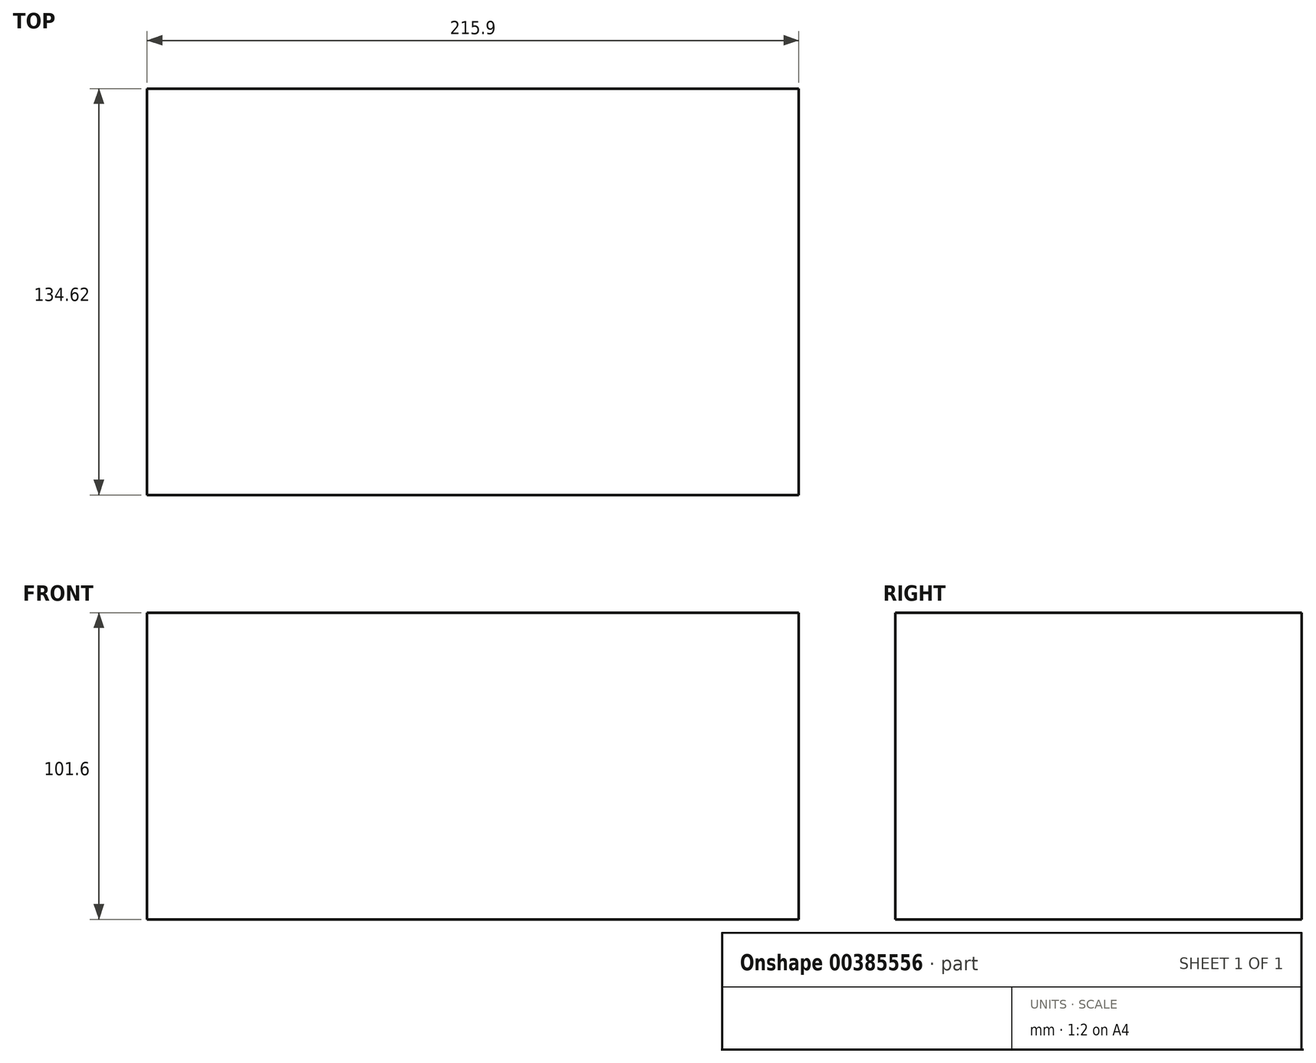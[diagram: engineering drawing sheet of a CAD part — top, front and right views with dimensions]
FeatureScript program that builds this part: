
annotation { "Feature Type Name" : "Feature", "Feature Type Description" : "" }
export const myFeature = defineFeature(function(context is Context, id is Id, definition is map)
    precondition{}
    {
        {
            var Q0;
            Q0=qCreatedBy(makeId("Top.planeOp"),FACE);
            var sketch = newSketch(context, id + "F0", { "sketchPlane" : qUnion([Q0])});
            skLineSegment(sketch, "E0.bottom", {"start": v(107.95, -67.3) * mm, "end": v(-107.95, -67.31) * mm});
            skLineSegment(sketch, "E0.top", {"start": v(107.95, 67.31) * mm, "end": v(-107.95, 67.31) * mm});
            skLineSegment(sketch, "E0.left", {"start": v(107.95, -67.3) * mm, "end": v(107.95, 67.31) * mm});
            skLineSegment(sketch, "E0.right", {"start": v(-107.95, -67.31) * mm, "end": v(-107.95, 67.31) * mm});
            skPoint(sketch, "E0.middle", {"position": v(0, 0) * mm});
            skSolve(sketch);
        }
        {
            var Q0;
            Q0=makeQuery(id+"F0.imprint","IMPRINT",FACE,{"disambiguationData":[TD([[makeQuery(id+"F0.imprint","IMPRINT",EDGE,{"derivedFrom":sQuery(id+"F0.wireOp",EDGE,"E0.bottom")}),-1.0]])]});
            extrude(context, id + "F1", {"entities" : qUnion([Q0]), "depth" : 101.6 * mm});
        }
    });
